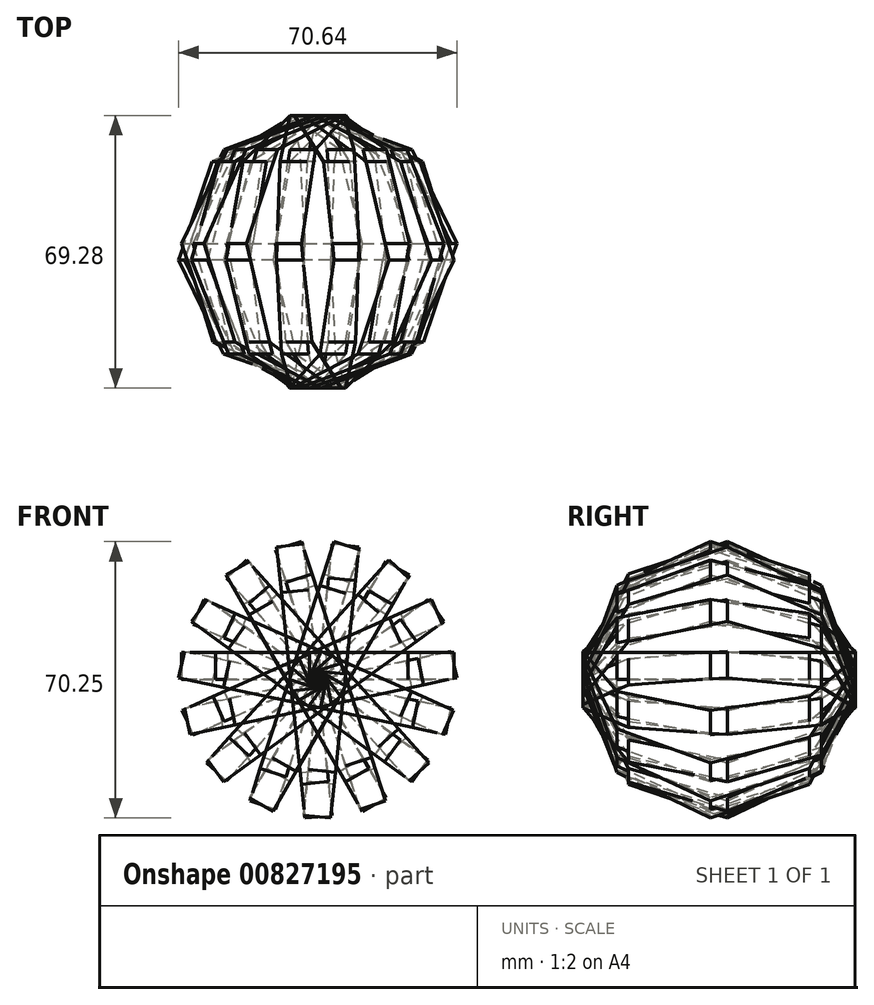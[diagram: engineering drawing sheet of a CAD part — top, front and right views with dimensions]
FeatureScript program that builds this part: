
annotation { "Feature Type Name" : "Feature", "Feature Type Description" : "" }
export const myFeature = defineFeature(function(context is Context, id is Id, definition is map)
    precondition{}
    {
        {
            var Q0;
            Q0=qCreatedBy(makeId("Top.planeOp"),FACE);
            var sketch = newSketch(context, id + "F0", { "sketchPlane" : qUnion([Q0])});
            skCircle(sketch, "E0.cCircle", {"center": v(0, 0) * mm, "radius": 32.06 * mm, "construction": true});
            skLineSegment(sketch, "E0.0", {"start": v(-22.98, 26.01) * mm, "end": v(2.15, 34.64) * mm});
            skLineSegment(sketch, "E0.1", {"start": v(2.15, 34.64) * mm, "end": v(26.01, 22.98) * mm});
            skLineSegment(sketch, "E0.2", {"start": v(26.01, 22.98) * mm, "end": v(34.64, -2.15) * mm});
            skLineSegment(sketch, "E0.3", {"start": v(34.64, -2.15) * mm, "end": v(22.98, -26.01) * mm});
            skLineSegment(sketch, "E0.4", {"start": v(22.98, -26.01) * mm, "end": v(-2.15, -34.64) * mm});
            skLineSegment(sketch, "E0.5", {"start": v(-2.15, -34.64) * mm, "end": v(-26.01, -22.98) * mm});
            skLineSegment(sketch, "E0.6", {"start": v(-26.01, -22.98) * mm, "end": v(-34.64, 2.15) * mm});
            skLineSegment(sketch, "E0.7", {"start": v(-34.64, 2.15) * mm, "end": v(-22.98, 26.01) * mm});
            skPoint(sketch, "E0.0.midPoint", {"position": v(-10.41, 30.33) * mm});
            skSolve(sketch);
        }
        {
            var Q0;
            Q0=qCreatedBy(makeId("Top.planeOp"),FACE);
            var sketch = newSketch(context, id + "F1", { "sketchPlane" : qUnion([Q0])});
            skLineSegment(sketch, "E1", {"start": v(0, -44.66) * mm, "end": v(0, 43.76) * mm});
            skSolve(sketch);
        }
        {
            var Q0;
            Q0=makeQuery(id+"F0.imprint","IMPRINT",FACE,{"disambiguationData":[TD([[makeQuery(id+"F0.imprint","IMPRINT",EDGE,{"derivedFrom":sQuery(id+"F0.wireOp",EDGE,"E0.0")}),-1.0]])]});
            extrude(context, id + "F2", {"entities" : qUnion([Q0]), "depth" : 6.9 * mm, "offsetDistance" : 25 * mm});
        }
        {
            var Q0;
            Q0=makeQuery(id+"F2.opExtrude","SWEPT_BODY",BODY,{"disambiguationData":[OSD([sQuery(id+"F0.wireOp",EDGE,"E0.0"),sQuery(id+"F0.wireOp",EDGE,"E0.1"),sQuery(id+"F0.wireOp",EDGE,"E0.2"),sQuery(id+"F0.wireOp",EDGE,"E0.3"),sQuery(id+"F0.wireOp",EDGE,"E0.4"),sQuery(id+"F0.wireOp",EDGE,"E0.5"),sQuery(id+"F0.wireOp",EDGE,"E0.6"),sQuery(id+"F0.wireOp",EDGE,"E0.7")])]});
            var Q1;
            Q1=sQuery(id+"F1.wireOp",EDGE,"E1");
            circularPattern(context, id + "F3", {"entities" : qUnion([Q0]), "axis" : qUnion([Q1]), "angle" : 360 * degree, "instanceCount" : 15, "equalSpace" : true, "isCentered" : true});
        }
    });
